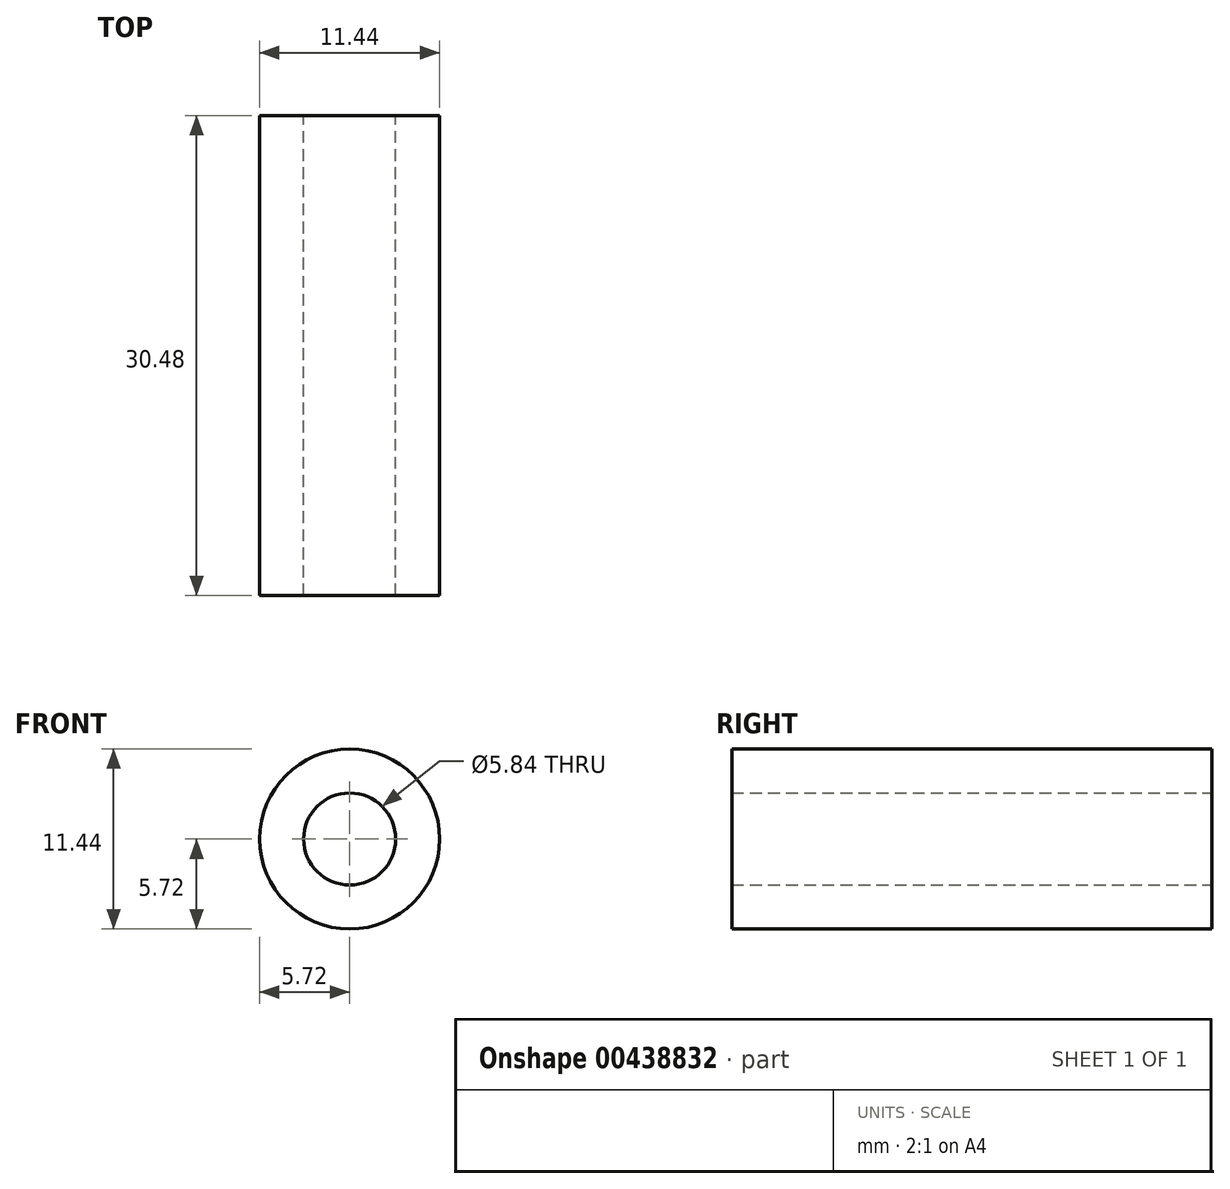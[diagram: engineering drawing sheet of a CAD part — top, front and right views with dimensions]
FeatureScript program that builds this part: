
annotation { "Feature Type Name" : "Feature", "Feature Type Description" : "" }
export const myFeature = defineFeature(function(context is Context, id is Id, definition is map)
    precondition{}
    {
        {
            var Q0;
            Q0=qCreatedBy(makeId("Front.planeOp"),FACE);
            var sketch = newSketch(context, id + "F0", { "sketchPlane" : qUnion([Q0])});
            skCircle(sketch, "E0", {"center": v(0, 0) * mm, "radius": 2.92 * mm});
            skCircle(sketch, "E1", {"center": v(0, 0) * mm, "radius": 5.72 * mm});
            skSolve(sketch);
        }
        {
            var Q0;
            Q0=makeQuery(id+"F0.imprint","IMPRINT",FACE,{"disambiguationData":[TD([[makeQuery(id+"F0.imprint","IMPRINT",EDGE,{"derivedFrom":sQuery(id+"F0.wireOp",EDGE,"E0")}),-1.0]])]});
            extrude(context, id + "F1", {"entities" : qUnion([Q0]), "depth" : 30.48 * mm});
        }
    });
